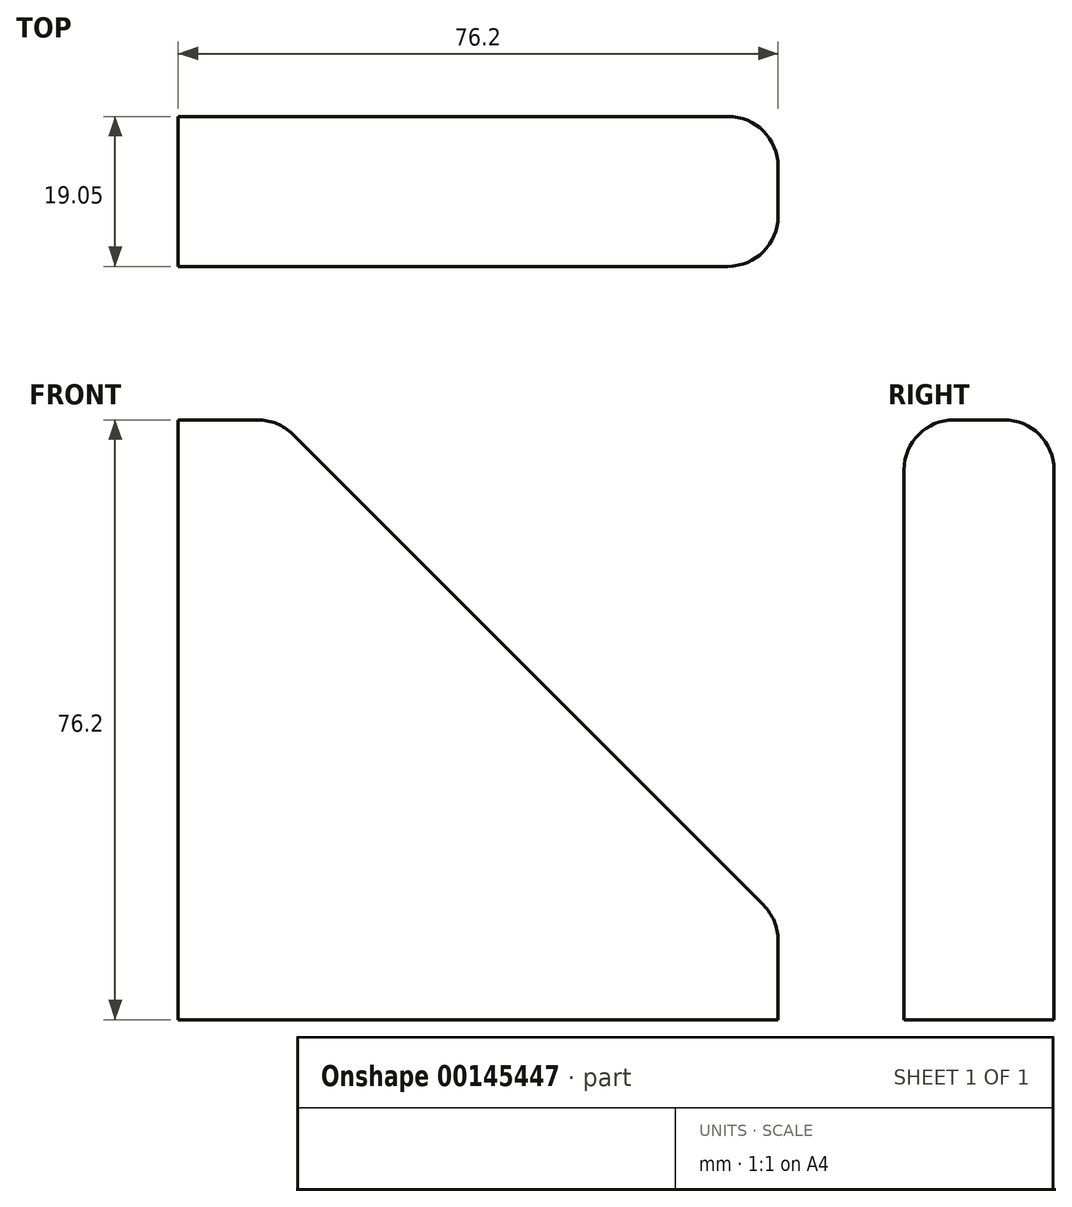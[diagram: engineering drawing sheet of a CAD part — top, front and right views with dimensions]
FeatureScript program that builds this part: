
annotation { "Feature Type Name" : "Feature", "Feature Type Description" : "" }
export const myFeature = defineFeature(function(context is Context, id is Id, definition is map)
    precondition{}
    {
        {
            var Q0;
            Q0=qCreatedBy(makeId("Front.planeOp"),FACE);
            var sketch = newSketch(context, id + "F0", { "sketchPlane" : qUnion([Q0])});
            skLineSegment(sketch, "E0", {"start": v(0, 0) * mm, "end": v(0, 76.2) * mm});
            skLineSegment(sketch, "E1", {"start": v(0, 76.2) * mm, "end": v(12.7, 76.2) * mm});
            skLineSegment(sketch, "E2", {"start": v(12.7, 76.2) * mm, "end": v(76.2, 12.7) * mm});
            skLineSegment(sketch, "E3", {"start": v(76.2, 12.7) * mm, "end": v(76.2, 0) * mm});
            skLineSegment(sketch, "E4", {"start": v(76.2, 0) * mm, "end": v(0, 0) * mm});
            skSolve(sketch);
        }
        {
            var Q0;
            Q0 = qSketchRegion(id + "F0", true);
            extrude(context, id + "F1", {"entities" : qUnion([Q0]), "depth" : 19.05 * mm});
        }
        {
            var Q0;
            Q0=makeQuery(id+"F1.opExtrude","SWEPT_EDGE",EDGE,{"disambiguationData":[OSD([sQuery(id+"F0.wireOp",EDGE,"E1"),sQuery(id+"F0.wireOp",EDGE,"E2")])]});
            var Q1;
            Q1=makeQuery(id+"F1.opExtrude","SWEPT_EDGE",EDGE,{"disambiguationData":[OSD([sQuery(id+"F0.wireOp",EDGE,"E2"),sQuery(id+"F0.wireOp",EDGE,"E3")])]});
            fillet(context, id + "F2", {"entities" : qUnion([Q0, Q1]), "radius" : 6.35 * mm, "tangentPropagation" : true, "allowEdgeOverflow" : false});
        }
        {
            var Q0;
            Q0=makeQuery(id+"F1.opExtrude","CAP_EDGE",EDGE,{"disambiguationData":[OSD([sQuery(id+"F0.wireOp",EDGE,"E2")])],"isStart":false});
            var Q1;
            Q1=makeQuery(id+"F1.opExtrude","CAP_EDGE",EDGE,{"disambiguationData":[OSD([sQuery(id+"F0.wireOp",EDGE,"E2")])],"isStart":true});
            fillet(context, id + "F3", {"entities" : qUnion([Q0, Q1]), "radius" : 6.35 * mm, "tangentPropagation" : true, "allowEdgeOverflow" : false});
        }
    });
